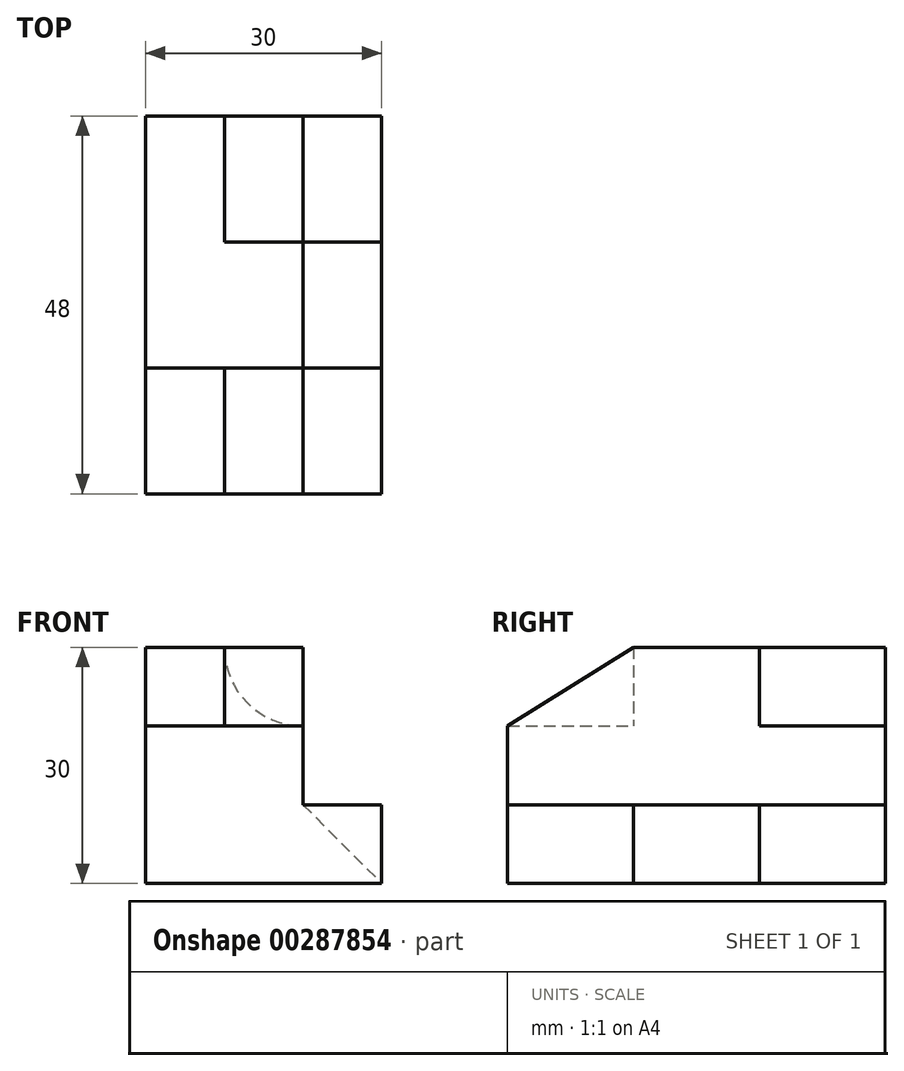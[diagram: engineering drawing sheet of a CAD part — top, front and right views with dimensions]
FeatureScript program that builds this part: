
annotation { "Feature Type Name" : "Feature", "Feature Type Description" : "" }
export const myFeature = defineFeature(function(context is Context, id is Id, definition is map)
    precondition{}
    {
        {
            var Q0;
            Q0=qCreatedBy(makeId("Front.planeOp"),FACE);
            var sketch = newSketch(context, id + "F0", { "sketchPlane" : qUnion([Q0])});
            skLineSegment(sketch, "E0.bottom", {"start": v(0, 0) * mm, "end": v(30, 0) * mm});
            skLineSegment(sketch, "E0.top", {"start": v(0, 30) * mm, "end": v(30, 30) * mm});
            skLineSegment(sketch, "E0.left", {"start": v(0, 0) * mm, "end": v(0, 30) * mm});
            skLineSegment(sketch, "E0.right", {"start": v(30, 0) * mm, "end": v(30, 30) * mm});
            skLineSegment(sketch, "E1.bottom", {"start": v(30, 30) * mm, "end": v(20, 30) * mm});
            skLineSegment(sketch, "E1.top", {"start": v(30, 10) * mm, "end": v(20, 10) * mm});
            skLineSegment(sketch, "E1.left", {"start": v(30, 30) * mm, "end": v(30, 10) * mm});
            skLineSegment(sketch, "E1.right", {"start": v(20, 30) * mm, "end": v(20, 10) * mm});
            skSolve(sketch);
        }
        {
            var Q0;
            Q0=makeQuery(id+"F0.imprint","IMPRINT",FACE,{"disambiguationData":[TD([[makeQuery(id+"F0.imprint","IMPRINT",EDGE,{"derivedFrom":sQuery(id+"F0.wireOp",EDGE,"E0.bottom")}),1.0]])]});
            extrude(context, id + "F1", {"entities" : qUnion([Q0]), "depth" : 48 * mm, "symmetric" : true});
        }
        {
            var Q0;
            Q0=qCreatedBy(makeId("Front.planeOp"),FACE);
            var sketch = newSketch(context, id + "F2", { "sketchPlane" : qUnion([Q0])});
            skLineSegment(sketch, "E2.0", {"start": v(30, 10) * mm, "end": v(20, 10) * mm});
            skLineSegment(sketch, "E3.0", {"start": v(30, 0) * mm, "end": v(30, 10) * mm});
            skLineSegment(sketch, "E4", {"start": v(20, 10) * mm, "end": v(30, 0) * mm});
            skSolve(sketch);
        }
        {
            var Q0;
            Q0 = qSketchRegion(id + "F2", true);
            extrude(context, id + "F3", {"entities" : qUnion([Q0]), "operationType" : NewBodyOperationType.REMOVE, "oppositeDirection" : true, "depth" : 16 * mm, "symmetric" : true});
        }
        {
            var Q0;
            Q0=makeQuery(id+"F1.opExtrude","SWEPT_FACE",FACE,{"disambiguationData":[OSD([sQuery(id+"F0.wireOp",EDGE,"E0.left")])]});
            var sketch = newSketch(context, id + "F4", { "sketchPlane" : qUnion([Q0])});
            skLineSegment(sketch, "E5.bottom", {"start": v(24, 30) * mm, "end": v(8, 30) * mm});
            skLineSegment(sketch, "E5.top", {"start": v(24, 20) * mm, "end": v(8, 20) * mm});
            skLineSegment(sketch, "E5.left", {"start": v(24, 30) * mm, "end": v(24, 20) * mm});
            skLineSegment(sketch, "E5.right", {"start": v(8, 30) * mm, "end": v(8, 20) * mm});
            skLineSegment(sketch, "E6", {"start": v(8, 30) * mm, "end": v(24, 20) * mm});
            skSolve(sketch);
        }
        {
            var Q0;
            Q0=makeQuery(id+"F4.imprint","IMPRINT",FACE,{"disambiguationData":[TD([[makeQuery(id+"F4.imprint","IMPRINT",EDGE,{"derivedFrom":sQuery(id+"F4.wireOp",EDGE,"E5.bottom")}),1.0]])]});
            extrude(context, id + "F5", {"entities" : qUnion([Q0]), "operationType" : NewBodyOperationType.REMOVE, "endBound" : BoundingType.THROUGH_ALL, "oppositeDirection" : true, "depth" : 25 * mm});
        }
        {
            var Q0;
            Q0=makeQuery(id+"F4.imprint","IMPRINT",FACE,{"disambiguationData":[TD([[makeQuery(id+"F4.imprint","IMPRINT",EDGE,{"derivedFrom":sQuery(id+"F4.wireOp",EDGE,"E5.top")}),-1.0]])]});
            extrude(context, id + "F6", {"entities" : qUnion([Q0]), "operationType" : NewBodyOperationType.REMOVE, "oppositeDirection" : true, "depth" : 10 * mm});
        }
        {
            var Q0;
            Q0=makeQuery(id+"F1.opExtrude","CAP_FACE",FACE,{"disambiguationData":[OSD([sQuery(id+"F0.wireOp",EDGE,"E0.bottom"),sQuery(id+"F0.wireOp",EDGE,"E0.top"),sQuery(id+"F0.wireOp",EDGE,"E0.left"),sQuery(id+"F0.wireOp",EDGE,"E0.right"),sQuery(id+"F0.wireOp",EDGE,"E1.top"),sQuery(id+"F0.wireOp",EDGE,"E1.right")])],"isStart":true});
            var sketch = newSketch(context, id + "F7", { "sketchPlane" : qUnion([Q0])});
            skCircle(sketch, "E7", {"center": v(-20, 30) * mm, "radius": 10 * mm});
            skSolve(sketch);
        }
        {
            var Q0;
            Q0 = qSketchRegion(id + "F7", true);
            extrude(context, id + "F8", {"entities" : qUnion([Q0]), "operationType" : NewBodyOperationType.REMOVE, "oppositeDirection" : true, "depth" : 16 * mm});
        }
    });
